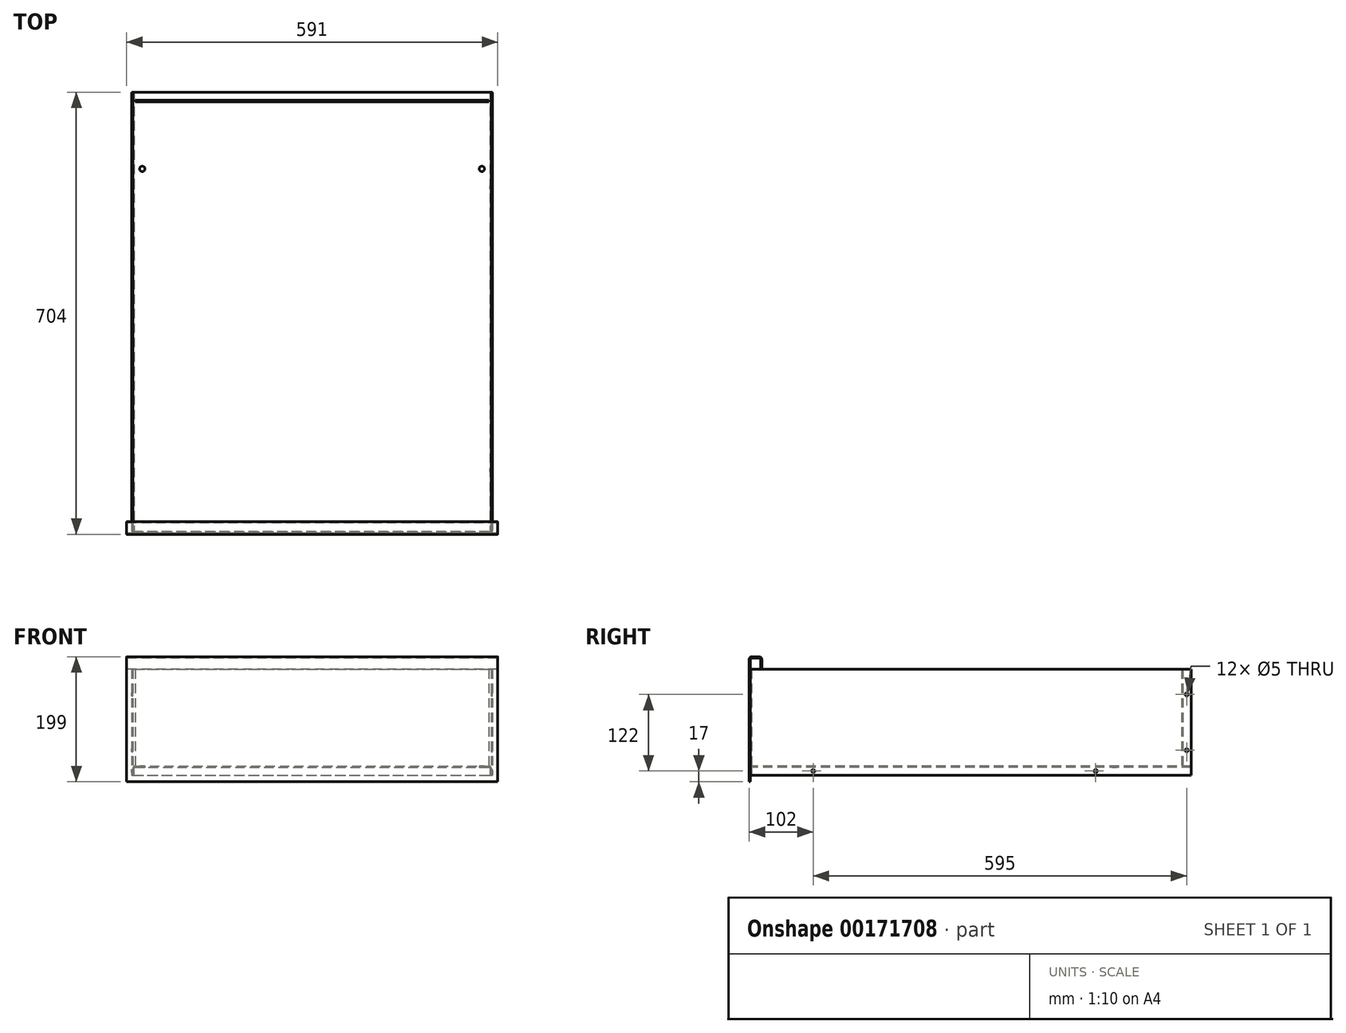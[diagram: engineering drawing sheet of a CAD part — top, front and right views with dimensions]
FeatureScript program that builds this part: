
annotation { "Feature Type Name" : "Feature", "Feature Type Description" : "" }
export const myFeature = defineFeature(function(context is Context, id is Id, definition is map)
    precondition{}
    {
        {
            var Q0;
            Q0=qCreatedBy(makeId("Top.planeOp"),FACE);
            var sketch = newSketch(context, id + "F0", { "sketchPlane" : qUnion([Q0])});
            skLineSegment(sketch, "E0.top", {"start": v(-283.5, -351) * mm, "end": v(283.5, -351) * mm});
            skLineSegment(sketch, "E0.left", {"start": v(-287.5, 351) * mm, "end": v(-287.5, -347) * mm});
            skLineSegment(sketch, "E0.right", {"start": v(287.5, 351) * mm, "end": v(287.5, -347) * mm});
            skPoint(sketch, "E0.middle", {"position": v(0, 0) * mm});
            skLineSegment(sketch, "E1", {"start": v(-287.5, 351) * mm, "end": v(287.5, 351) * mm, "construction": true});
            skLineSegment(sketch, "E2", {"start": v(-287.5, 351) * mm, "end": v(-285.5, 351) * mm});
            skLineSegment(sketch, "E3", {"start": v(-285.5, 351) * mm, "end": v(-285.5, -349) * mm});
            skLineSegment(sketch, "E4", {"start": v(-285.5, -349) * mm, "end": v(285.5, -349) * mm});
            skLineSegment(sketch, "E5", {"start": v(285.5, -349) * mm, "end": v(285.5, 351) * mm});
            skPoint(sketch, "E6.visualSharp", {"position": v(-287.5, -351) * mm});
            skArc(sketch, "E6.filletArc", {"start": v(-287.5, -347) * mm, "mid": v(-286.33, -349.83) * mm, "end": v(-283.5, -351) * mm});
            skPoint(sketch, "E7.visualSharp", {"position": v(287.5, -351) * mm});
            skArc(sketch, "E7.filletArc", {"start": v(283.5, -351) * mm, "mid": v(286.33, -349.83) * mm, "end": v(287.5, -347) * mm});
            skLineSegment(sketch, "E8", {"start": v(285.5, 351) * mm, "end": v(287.5, 351) * mm});
            skSolve(sketch);
        }
        {
            var Q0;
            Q0=makeQuery(id+"F0.imprint","IMPRINT",FACE,{"disambiguationData":[TD([[makeQuery(id+"F0.imprint","IMPRINT",EDGE,{"derivedFrom":sQuery(id+"F0.wireOp",EDGE,"E0.top")}),1.0]])]});
            extrude(context, id + "F1", {"entities" : qUnion([Q0]), "depth" : 169 * mm});
        }
        {
            var Q0;
            Q0=makeQuery(id+"F1.opExtrude","SWEPT_FACE",FACE,{"disambiguationData":[OSD([sQuery(id+"F0.wireOp",EDGE,"E4")])]});
            var sketch = newSketch(context, id + "F2", { "sketchPlane" : qUnion([Q0])});
            skLineSegment(sketch, "E9", {"start": v(-285.5, 0) * mm, "end": v(-285.5, 11) * mm});
            skLineSegment(sketch, "E10", {"start": v(-281.5, 15) * mm, "end": v(281.5, 15) * mm});
            skLineSegment(sketch, "E11", {"start": v(285.5, 11) * mm, "end": v(285.5, 0) * mm});
            skLineSegment(sketch, "E12", {"start": v(285.5, 0) * mm, "end": v(283.5, 0) * mm});
            skLineSegment(sketch, "E13", {"start": v(283.5, 0) * mm, "end": v(283.5, 13) * mm});
            skLineSegment(sketch, "E14", {"start": v(283.5, 13) * mm, "end": v(-283.5, 13) * mm});
            skLineSegment(sketch, "E15", {"start": v(-283.5, 13) * mm, "end": v(-283.5, 0) * mm});
            skLineSegment(sketch, "E16", {"start": v(-283.5, 0) * mm, "end": v(-285.5, 0) * mm});
            skPoint(sketch, "E17.visualSharp", {"position": v(285.5, 15) * mm});
            skArc(sketch, "E17.filletArc", {"start": v(285.5, 11) * mm, "mid": v(284.33, 13.83) * mm, "end": v(281.5, 15) * mm});
            skPoint(sketch, "E18.visualSharp", {"position": v(-285.5, 15) * mm});
            skArc(sketch, "E18.filletArc", {"start": v(-281.5, 15) * mm, "mid": v(-284.33, 13.83) * mm, "end": v(-285.5, 11) * mm});
            skSolve(sketch);
        }
        {
            var Q0;
            Q0=makeQuery(id+"F2.imprint","IMPRINT",FACE,{"disambiguationData":[TD([[makeQuery(id+"F2.imprint","IMPRINT",EDGE,{"derivedFrom":sQuery(id+"F2.wireOp",EDGE,"E9")}),1.0]])]});
            var Q1;
            Q1=makeQuery(id+"F1.opExtrude","SWEPT_FACE",FACE,{"disambiguationData":[OSD([sQuery(id+"F0.wireOp",EDGE,"E2")])]});
            extrude(context, id + "F3", {"entities" : qUnion([Q0]), "endBound" : BoundingType.UP_TO_SURFACE, "endBoundEntityFace" : qUnion([Q1]), "depth" : 25 * mm});
        }
        {
            var Q0;
            Q0=makeQuery(id+"F3.opExtrude","SWEPT_FACE",FACE,{"disambiguationData":[OSD([sQuery(id+"F2.wireOp",EDGE,"E10")])]});
            var sketch = newSketch(context, id + "F4", { "sketchPlane" : qUnion([Q0])});
            skLineSegment(sketch, "E19.0", {"start": v(285.5, -349) * mm, "end": v(285.5, 351) * mm});
            skLineSegment(sketch, "E20.0", {"start": v(-285.5, 351) * mm, "end": v(-285.5, -349) * mm});
            skLineSegment(sketch, "E21", {"start": v(-285.5, 351) * mm, "end": v(-285.5, 340) * mm});
            skLineSegment(sketch, "E22", {"start": v(-281.5, 336) * mm, "end": v(281.5, 336) * mm});
            skLineSegment(sketch, "E23", {"start": v(285.5, 340) * mm, "end": v(285.5, 351) * mm});
            skLineSegment(sketch, "E24", {"start": v(285.5, 351) * mm, "end": v(283.5, 351) * mm});
            skLineSegment(sketch, "E25", {"start": v(283.5, 351) * mm, "end": v(283.5, 338) * mm});
            skLineSegment(sketch, "E26", {"start": v(283.5, 338) * mm, "end": v(-283.5, 338) * mm});
            skLineSegment(sketch, "E27", {"start": v(-283.5, 338) * mm, "end": v(-283.5, 351) * mm});
            skLineSegment(sketch, "E28", {"start": v(-283.5, 351) * mm, "end": v(-285.5, 351) * mm});
            skPoint(sketch, "E29.visualSharp", {"position": v(285.5, 336) * mm});
            skArc(sketch, "E29.filletArc", {"start": v(281.5, 336) * mm, "mid": v(284.33, 337.17) * mm, "end": v(285.5, 340) * mm});
            skPoint(sketch, "E30.visualSharp", {"position": v(-285.5, 336) * mm});
            skArc(sketch, "E30.filletArc", {"start": v(-285.5, 340) * mm, "mid": v(-284.33, 337.17) * mm, "end": v(-281.5, 336) * mm});
            skSolve(sketch);
        }
        {
            var Q0;
            {var subQ0=sQuery(id+"F4.wireOp",EDGE,"E22");Q0=makeQuery(id+"F4.imprint","IMPRINT",FACE,{"disambiguationData":[TD([[makeQuery(id+"F4.imprint","IMPRINT",EDGE,{"derivedFrom":subQ0}),1.0]])]});}
            var Q1;
            Q1=makeQuery(id+"F4.imprint","IMPRINT",FACE,{"disambiguationData":[TD([[makeQuery(id+"F4.imprint","IMPRINT",EDGE,{"derivedFrom":sQuery(id+"F4.wireOp",EDGE,"E21")}),1.0]])]});
            var Q2;
            Q2=makeQuery(id+"F4.imprint","IMPRINT",FACE,{"disambiguationData":[TD([[makeQuery(id+"F4.imprint","IMPRINT",EDGE,{"derivedFrom":sQuery(id+"F4.wireOp",EDGE,"E23")}),1.0]])]});
            var Q3;
            Q3=makeQuery(id+"F1.opExtrude","CAP_FACE",FACE,{"disambiguationData":[OSD([sQuery(id+"F0.wireOp",EDGE,"E0.top"),sQuery(id+"F0.wireOp",EDGE,"E0.left"),sQuery(id+"F0.wireOp",EDGE,"E0.right"),sQuery(id+"F0.wireOp",EDGE,"E2"),sQuery(id+"F0.wireOp",EDGE,"E3"),sQuery(id+"F0.wireOp",EDGE,"E4"),sQuery(id+"F0.wireOp",EDGE,"E5"),sQuery(id+"F0.wireOp",EDGE,"E6.filletArc"),sQuery(id+"F0.wireOp",EDGE,"E7.filletArc"),sQuery(id+"F0.wireOp",EDGE,"E8")])],"isStart":false});
            extrude(context, id + "F5", {"entities" : qUnion([Q0, Q1, Q2]), "endBound" : BoundingType.UP_TO_SURFACE, "endBoundEntityFace" : qUnion([Q3]), "depth" : 25 * mm});
        }
        {
            var Q0;
            Q0=makeQuery(id+"F1.opExtrude","SWEPT_FACE",FACE,{"disambiguationData":[OSD([sQuery(id+"F0.wireOp",EDGE,"E0.right")])]});
            var sketch = newSketch(context, id + "F6", { "sketchPlane" : qUnion([Q0])});
            skLineSegment(sketch, "E31.0", {"start": v(-351, 169) * mm, "end": v(-351, 0) * mm});
            skLineSegment(sketch, "E32", {"start": v(-374.1, 7) * mm, "end": v(407.57, 7) * mm, "construction": true});
            skLineSegment(sketch, "E33", {"start": v(344, -59.87) * mm, "end": v(344, 378.9) * mm, "construction": true});
            skPoint(sketch, "E34", {"position": v(-251, 7) * mm});
            skPoint(sketch, "E35", {"position": v(199, 7) * mm});
            skPoint(sketch, "E36", {"position": v(344, 129) * mm});
            skPoint(sketch, "E37", {"position": v(344, 40) * mm});
            skSolve(sketch);
        }
        {
            var Q0;
            Q0=sQuery(id+"F6.wireOp",VERTEX,"E37");
            var Q1;
            Q1=sQuery(id+"F6.wireOp",VERTEX,"E35");
            var Q2;
            Q2=sQuery(id+"F6.wireOp",VERTEX,"E36");
            var Q3;
            Q3=sQuery(id+"F6.wireOp",VERTEX,"E34");
            var Q4;
            Q4=makeQuery(id+"F1.opExtrude","SWEPT_BODY",BODY,{"disambiguationData":[OSD([sQuery(id+"F0.wireOp",EDGE,"E0.top"),sQuery(id+"F0.wireOp",EDGE,"E0.left"),sQuery(id+"F0.wireOp",EDGE,"E0.right"),sQuery(id+"F0.wireOp",EDGE,"E2"),sQuery(id+"F0.wireOp",EDGE,"E3"),sQuery(id+"F0.wireOp",EDGE,"E4"),sQuery(id+"F0.wireOp",EDGE,"E5"),sQuery(id+"F0.wireOp",EDGE,"E6.filletArc"),sQuery(id+"F0.wireOp",EDGE,"E7.filletArc"),sQuery(id+"F0.wireOp",EDGE,"E8")])]});
            var Q5;
            Q5=makeQuery(id+"F3.opExtrude","SWEPT_BODY",BODY,{"disambiguationData":[OSD([sQuery(id+"F2.wireOp",EDGE,"E9"),sQuery(id+"F2.wireOp",EDGE,"E10"),sQuery(id+"F2.wireOp",EDGE,"E11"),sQuery(id+"F2.wireOp",EDGE,"E12"),sQuery(id+"F2.wireOp",EDGE,"E13"),sQuery(id+"F2.wireOp",EDGE,"E14"),sQuery(id+"F2.wireOp",EDGE,"E15"),sQuery(id+"F2.wireOp",EDGE,"E16"),sQuery(id+"F2.wireOp",EDGE,"E17.filletArc"),sQuery(id+"F2.wireOp",EDGE,"E18.filletArc")])]});
            var Q6;
            Q6=makeQuery(id+"F5.opExtrude","SWEPT_BODY",BODY,{"disambiguationData":[OSD([sQuery(id+"F4.wireOp",EDGE,"E21"),sQuery(id+"F4.wireOp",EDGE,"E22"),sQuery(id+"F4.wireOp",EDGE,"E23"),sQuery(id+"F4.wireOp",EDGE,"E24"),sQuery(id+"F4.wireOp",EDGE,"E25"),sQuery(id+"F4.wireOp",EDGE,"E26"),sQuery(id+"F4.wireOp",EDGE,"E27"),sQuery(id+"F4.wireOp",EDGE,"E28"),sQuery(id+"F4.wireOp",EDGE,"E29.filletArc"),sQuery(id+"F4.wireOp",EDGE,"E30.filletArc")])]});
            hole(context, id + "F7", {"style" : HoleStyle.C_SINK, "endStyle" : HoleEndStyle.BLIND, "holeDiameter" : 5 * mm, "cSinkDiameter" : 5 * mm, "cSinkAngle" : 90 * degree, "holeDepth" : 2000 * mm, "startFromSketch" : true, "locations" : qUnion([Q0, Q1, Q2, Q3]), "scope" : qUnion([Q4, Q5, Q6])});
        }
        {
            var Q0;
            Q0=qCreatedBy(makeId("Right.planeOp"),FACE);
            var sketch = newSketch(context, id + "F8", { "sketchPlane" : qUnion([Q0])});
            skPoint(sketch, "E38.0", {"position": v(-351, 169) * mm});
            skPoint(sketch, "E39.0", {"position": v(-351, 0) * mm});
            skLineSegment(sketch, "E40.0", {"start": v(351, 169) * mm, "end": v(-347, 169) * mm});
            skLineSegment(sketch, "E41", {"start": v(-351, 169) * mm, "end": v(-351, 187) * mm});
            skLineSegment(sketch, "E42", {"start": v(-351, 187) * mm, "end": v(-335, 187) * mm});
            skLineSegment(sketch, "E43", {"start": v(-335, 187) * mm, "end": v(-335, 169) * mm});
            skLineSegment(sketch, "E44", {"start": v(-335, 169) * mm, "end": v(-333, 169) * mm});
            skLineSegment(sketch, "E45", {"start": v(-333, 169) * mm, "end": v(-333, 185) * mm});
            skLineSegment(sketch, "E46", {"start": v(-337, 189) * mm, "end": v(-349, 189) * mm});
            skLineSegment(sketch, "E47", {"start": v(-353, 185) * mm, "end": v(-353, 169) * mm});
            skLineSegment(sketch, "E48", {"start": v(-353, 169) * mm, "end": v(-351, 169) * mm});
            skPoint(sketch, "E49.visualSharp", {"position": v(-353, 189) * mm});
            skArc(sketch, "E49.filletArc", {"start": v(-349, 189) * mm, "mid": v(-351.83, 187.83) * mm, "end": v(-353, 185) * mm});
            skPoint(sketch, "E50.visualSharp", {"position": v(-333, 189) * mm});
            skArc(sketch, "E50.filletArc", {"start": v(-333, 185) * mm, "mid": v(-334.17, 187.83) * mm, "end": v(-337, 189) * mm});
            skLineSegment(sketch, "E51", {"start": v(-351, 0) * mm, "end": v(-351, -10) * mm});
            skLineSegment(sketch, "E52", {"start": v(-351, -10) * mm, "end": v(-353, -10) * mm});
            skLineSegment(sketch, "E53", {"start": v(-353, -10) * mm, "end": v(-353, 0) * mm});
            skLineSegment(sketch, "E54", {"start": v(-353, 0) * mm, "end": v(-351, 0) * mm});
            skLineSegment(sketch, "E55", {"start": v(-351, 0) * mm, "end": v(-351, 169) * mm});
            skLineSegment(sketch, "E56", {"start": v(-353, 169) * mm, "end": v(-353, 0) * mm});
            skSolve(sketch);
        }
        {
            var Q0;
            Q0=makeQuery(id+"F8.imprint","IMPRINT",FACE,{"disambiguationData":[TD([[makeQuery(id+"F8.imprint","IMPRINT",EDGE,{"derivedFrom":sQuery(id+"F8.wireOp",EDGE,"E51")}),-1.0]])]});
            var Q1;
            Q1=makeQuery(id+"F8.imprint","IMPRINT",FACE,{"disambiguationData":[TD([[makeQuery(id+"F8.imprint","IMPRINT",EDGE,{"derivedFrom":sQuery(id+"F8.wireOp",EDGE,"E48")}),-1.0]])]});
            var Q2;
            Q2=makeQuery(id+"F8.imprint","IMPRINT",FACE,{"disambiguationData":[TD([[makeQuery(id+"F8.imprint","IMPRINT",EDGE,{"derivedFrom":sQuery(id+"F8.wireOp",EDGE,"E41")}),1.0]])]});
            extrude(context, id + "F9", {"entities" : qUnion([Q0, Q1, Q2]), "endBound" : BoundingType.SYMMETRIC, "depth" : 591 * mm});
        }
        {
            var Q0;
            Q0=makeQuery(id+"F3.opExtrude","SWEPT_FACE",FACE,{"disambiguationData":[OSD([sQuery(id+"F2.wireOp",EDGE,"E14")])]});
            var sketch = newSketch(context, id + "F10", { "sketchPlane" : qUnion([Q0])});
            skLineSegment(sketch, "E57", {"start": v(412.81, -229) * mm, "end": v(-462.02, -229) * mm, "construction": true});
            skLineSegment(sketch, "E58.0", {"start": v(285.5, 349) * mm, "end": v(285.5, -351) * mm});
            skLineSegment(sketch, "E59.0", {"start": v(-285.5, -351) * mm, "end": v(-285.5, 349) * mm});
            skPoint(sketch, "E60", {"position": v(-270.5, -229) * mm});
            skPoint(sketch, "E61", {"position": v(270.5, -229) * mm});
            skSolve(sketch);
        }
        {
            var Q0;
            Q0=sQuery(id+"F10.wireOp",VERTEX,"E61");
            var Q1;
            Q1=sQuery(id+"F10.wireOp",VERTEX,"E60");
            var Q2;
            Q2=makeQuery(id+"F3.opExtrude","SWEPT_BODY",BODY,{"disambiguationData":[OSD([sQuery(id+"F2.wireOp",EDGE,"E9"),sQuery(id+"F2.wireOp",EDGE,"E10"),sQuery(id+"F2.wireOp",EDGE,"E11"),sQuery(id+"F2.wireOp",EDGE,"E12"),sQuery(id+"F2.wireOp",EDGE,"E13"),sQuery(id+"F2.wireOp",EDGE,"E14"),sQuery(id+"F2.wireOp",EDGE,"E15"),sQuery(id+"F2.wireOp",EDGE,"E16"),sQuery(id+"F2.wireOp",EDGE,"E17.filletArc"),sQuery(id+"F2.wireOp",EDGE,"E18.filletArc")])]});
            hole(context, id + "F11", {"style" : HoleStyle.C_SINK, "endStyle" : HoleEndStyle.BLIND, "holeDiameter" : 8.5 * mm, "cSinkDiameter" : 8.5 * mm, "cSinkAngle" : 90 * degree, "holeDepth" : 20 * mm, "startFromSketch" : true, "locations" : qUnion([Q0, Q1]), "scope" : qUnion([Q2])});
        }
    });
